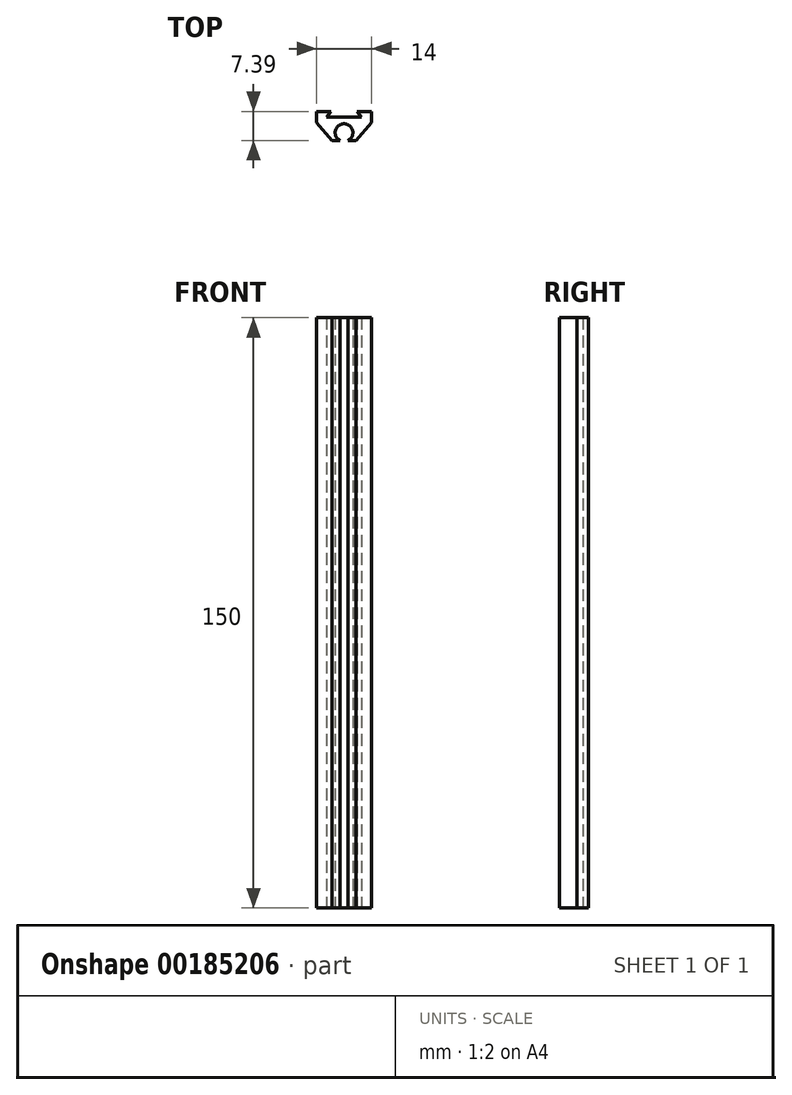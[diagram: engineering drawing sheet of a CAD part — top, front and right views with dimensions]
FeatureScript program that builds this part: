
annotation { "Feature Type Name" : "Feature", "Feature Type Description" : "" }
export const myFeature = defineFeature(function(context is Context, id is Id, definition is map)
    precondition{}
    {
        {
            var Q0;
            Q0=qCreatedBy(makeId("Top.planeOp"),FACE);
            var sketch = newSketch(context, id + "F0", { "sketchPlane" : qUnion([Q0])});
            skLineSegment(sketch, "E0.bottom", {"start": v(7, -3.59) * mm, "end": v(-7, -3.59) * mm});
            skLineSegment(sketch, "E0.top", {"start": v(7, -5.09) * mm, "end": v(-7, -5.09) * mm});
            skLineSegment(sketch, "E0.left", {"start": v(7, -3.59) * mm, "end": v(7, -5.09) * mm});
            skLineSegment(sketch, "E0.right", {"start": v(-7, -3.59) * mm, "end": v(-7, -5.09) * mm});
            skPoint(sketch, "E0.middle", {"position": v(0, -4.34) * mm});
            skLineSegment(sketch, "E1", {"start": v(0, 2.23) * mm, "end": v(0, -20.15) * mm, "construction": true});
            skArc(sketch, "E2", {"start": v(1, -9.6) * mm, "mid": v(0, -5.34) * mm, "end": v(-1, -9.6) * mm});
            skLineSegment(sketch, "E3", {"start": v(-1, -9.6) * mm, "end": v(-3, -9.6) * mm});
            skLineSegment(sketch, "E4", {"start": v(-3, -9.6) * mm, "end": v(-7, -5.09) * mm});
            skLineSegment(sketch, "E5", {"start": v(1, -9.6) * mm, "end": v(3, -9.6) * mm});
            skLineSegment(sketch, "E6", {"start": v(3, -9.6) * mm, "end": v(7, -5.09) * mm});
            skLineSegment(sketch, "E7", {"start": v(-4.5, -3.59) * mm, "end": v(-3.34, -2.2) * mm});
            skLineSegment(sketch, "E8", {"start": v(-3.34, -2.2) * mm, "end": v(-7, -2.2) * mm});
            skLineSegment(sketch, "E9", {"start": v(-7, -2.2) * mm, "end": v(-7, -3.59) * mm});
            skLineSegment(sketch, "E10.MirrorCS", {"start": v(7, -2.2) * mm, "end": v(7, -3.59) * mm});
            skLineSegment(sketch, "E11.MirrorCS", {"start": v(4.5, -3.59) * mm, "end": v(3.34, -2.2) * mm});
            skLineSegment(sketch, "E12.MirrorCS", {"start": v(3.34, -2.2) * mm, "end": v(7, -2.2) * mm});
            skSolve(sketch);
        }
        {
            var Q0;
            Q0=qSketchRegion(id+"F0",true);
            extrude(context, id + "F1", {"entities" : qUnion([Q0]), "depth" : 150 * mm});
        }
    });
